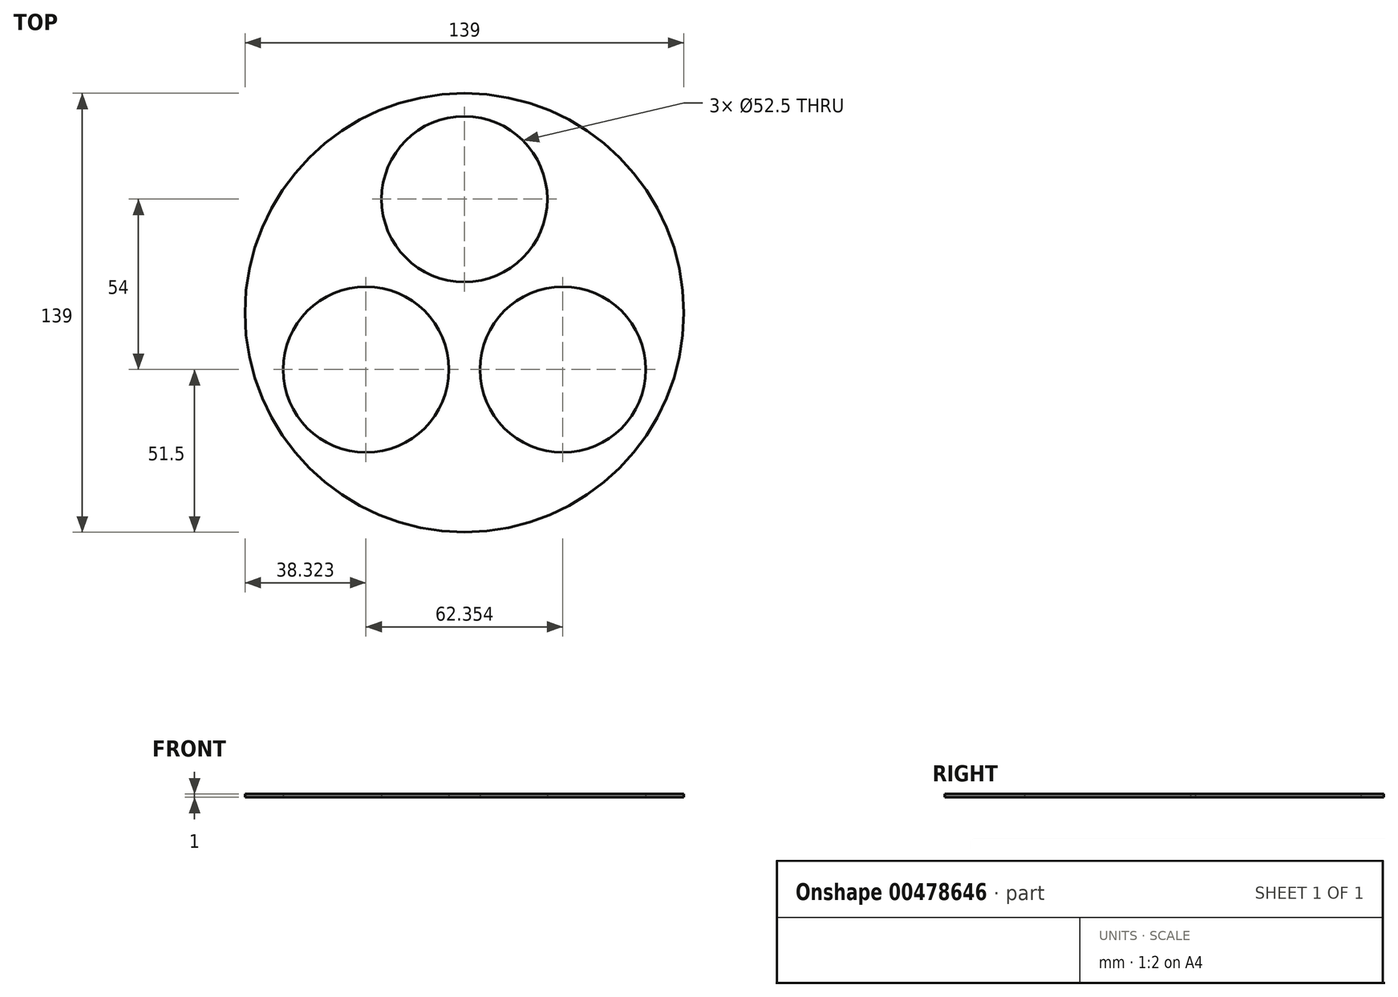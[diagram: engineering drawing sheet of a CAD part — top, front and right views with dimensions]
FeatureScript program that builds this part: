
annotation { "Feature Type Name" : "Feature", "Feature Type Description" : "" }
export const myFeature = defineFeature(function(context is Context, id is Id, definition is map)
    precondition{}
    {
        {
            var Q0;
            Q0=qCreatedBy(makeId("Top.planeOp"),FACE);
            var sketch = newSketch(context, id + "F0", { "sketchPlane" : qUnion([Q0])});
            skCircle(sketch, "E0", {"center": v(0, 0) * mm, "radius": 69.5 * mm});
            skCircle(sketch, "E1", {"center": v(0, 36) * mm, "radius": 26.25 * mm});
            skCircle(sketch, "E2.1.0", {"center": v(-31.18, -18) * mm, "radius": 26.25 * mm});
            skCircle(sketch, "E2.2.0", {"center": v(31.18, -18) * mm, "radius": 26.25 * mm});
            skSolve(sketch);
        }
        {
            var Q0;
            Q0 = qSketchRegion(id + "F0", true);
            extrude(context, id + "F1", {"entities" : qUnion([Q0]), "depth" : 1 * mm});
        }
    });
